# Revit family: Accessory-Flush_Actuator_Plate-KOHLER-PEBBLE-K-5413IN_1
name_source: partatom
category: Specialty Equipment
revit_build: Autodesk Revit 2017 (Build: 20160225_1515(x64)
units: mm (PartAtom-declared; Revit-internal decimal feet)

## family parameters
Cut with Voids When Loaded = No
Host = Face
OmniClass Number = 23.31.25.00
OmniClass Title = Toilet and Bath Specialties
Part Type = Normal
Room Calculation Point = No
Round Connector Dimension = Use Diameter
Shared = No

## types (3) — shared parameters
ADA Compliant = No
Assembly Code = C1030200
Date Modified = 01/05/2020
Default Elevation = 42"
Finish = Kohler-Metal-CP-Polished_Chrome
Height = 6 5/16"
Length = 9/16"
Manufacturer = KOHLER Co.
Master Format 2014 = 40 05 57.13
Master Format 2014 Name = Manual Actuators
Material = Premium Metal Construction
Product Name = PEBBLE
URL = https://www.kohler.co.in
WaterSense Certified = No
Width = 8 7/8"

## per-type parameters (varying)
| type | Description | Model | Product Documentation Link | Product Page URL | Type |
| CP-Polished Chrome | CHROME FACEPLATE | K-5413IN-CP |  |  | 1 |
| Mechanical Actuator, CP-Polished Chrome | FACEPLATE POLISHED CHROME | K-5413IN-M-CP |  |  | 2 |
| Pneumatic Actuator, CP-Polished Chrome | FACE PLATE FOR INWALL TANK | K-5413IN-P-CP | http://resources.kohler.com | https://www.kohler.co.in | 3 |

## geometry (parser evidence)
native form markers: Sweep x4
no freeform markers — native parametric forms only
